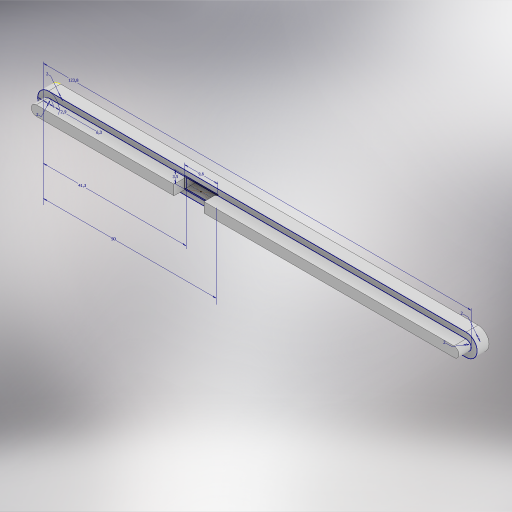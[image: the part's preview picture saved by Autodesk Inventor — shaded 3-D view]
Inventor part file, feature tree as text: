
AUTODESK INVENTOR PART (.ipt)
format: ipt  version: 2024 (Build 280153000, 153)  size: 429,568 bytes
history: native  units: mm
features: extrude x8, fillet x6, pattern_linear x4, other x3, sketch x2, chamfer x1
ambient origin geometry x8: Origin, YZ Plane, XZ Plane, XY Plane, X Axis, Y Axis, Z Axis, Center Point
bodies: Solid1 (feature_tree)
feature tree (24):
  other  "Table"
  other  "dvddrive-01"
  other  "dvddrive-02"
  sketch  "Sketch1"  dims[d0=2.9mm d1=123.8mm]
  extrude  "Extrusion1"  Depth=2.9mm
  extrude  "Extrusion2"  Depth=6.3mm
  extrude  "Extrusion3"  Depth=3.5mm TaperAngle=0.0deg
  extrude  "Extrusion4"  Depth=1.0mm
  chamfer  "Chamfer1"  Distance=50.0mm
  sketch  "Sketch3"  dims[d2=3.5mm d3=0.0mm d4=6.3mm d5=3.5mm d6=0.0mm d7=41.3mm d8=50.0mm d9=9.6mm d10=3.5mm d11=3.5mm d12=0.0mm d13=3.5mm d14=0.0mm d15=0.45mm d16=2.0mm d17=45.0deg d18=2.0mm d19=0.0mm d20=0.0mm d21=180.0mm d23=4.0mm d24=2.0mm d25=0.0mm d26=0.0mm d27=1.0mm d28=1.0mm d29=0.2mm d30=0.2mm d31=100.0mm d33=4.0mm d34=2.0mm d35=2.5mm d36=0.0mm d37=1.0mm d38=2.0mm d39=2.5mm d40=0.0mm d41=1.0mm d42=120.0mm d44=6.0mm d45=70.0mm d47=6.0mm]
  extrude  "Extrusion5"  Depth=9.6mm
  fillet  "Fillet2"  Radius=3.5mm
  fillet  "Fillet3"  Radius=3.5mm
  pattern_linear  "Rectangular Pattern1"  Spacing1=3.5mm  [1 undecoded]
  extrude  "Extrusion6"  Depth=0.45mm TaperAngle=45.0deg
  fillet  "Fillet1"  Radius=2.0mm
  fillet  "Fillet4"  [1 undecoded]
  pattern_linear  "Rectangular Pattern2"  Count1=18 Spacing1=4.0mm
  extrude  "Extrusion7"  Depth=2.0mm
  fillet  "Fillet5"  [1 undecoded]
  extrude  "Extrusion8"  Depth=1.0mm
  fillet  "Fillet6"  Radius=1.0mm
  pattern_linear  "Rectangular Pattern3"  Spacing1=0.2mm  [1 undecoded]
  pattern_linear  "Rectangular Pattern4"  Spacing1=0.2mm  [1 undecoded]
note: 5 required parameter values undecoded (feature->parameter linkage not recoverable at this tier; creation-order binding heuristic only, values carry confidence <= 0.55)
